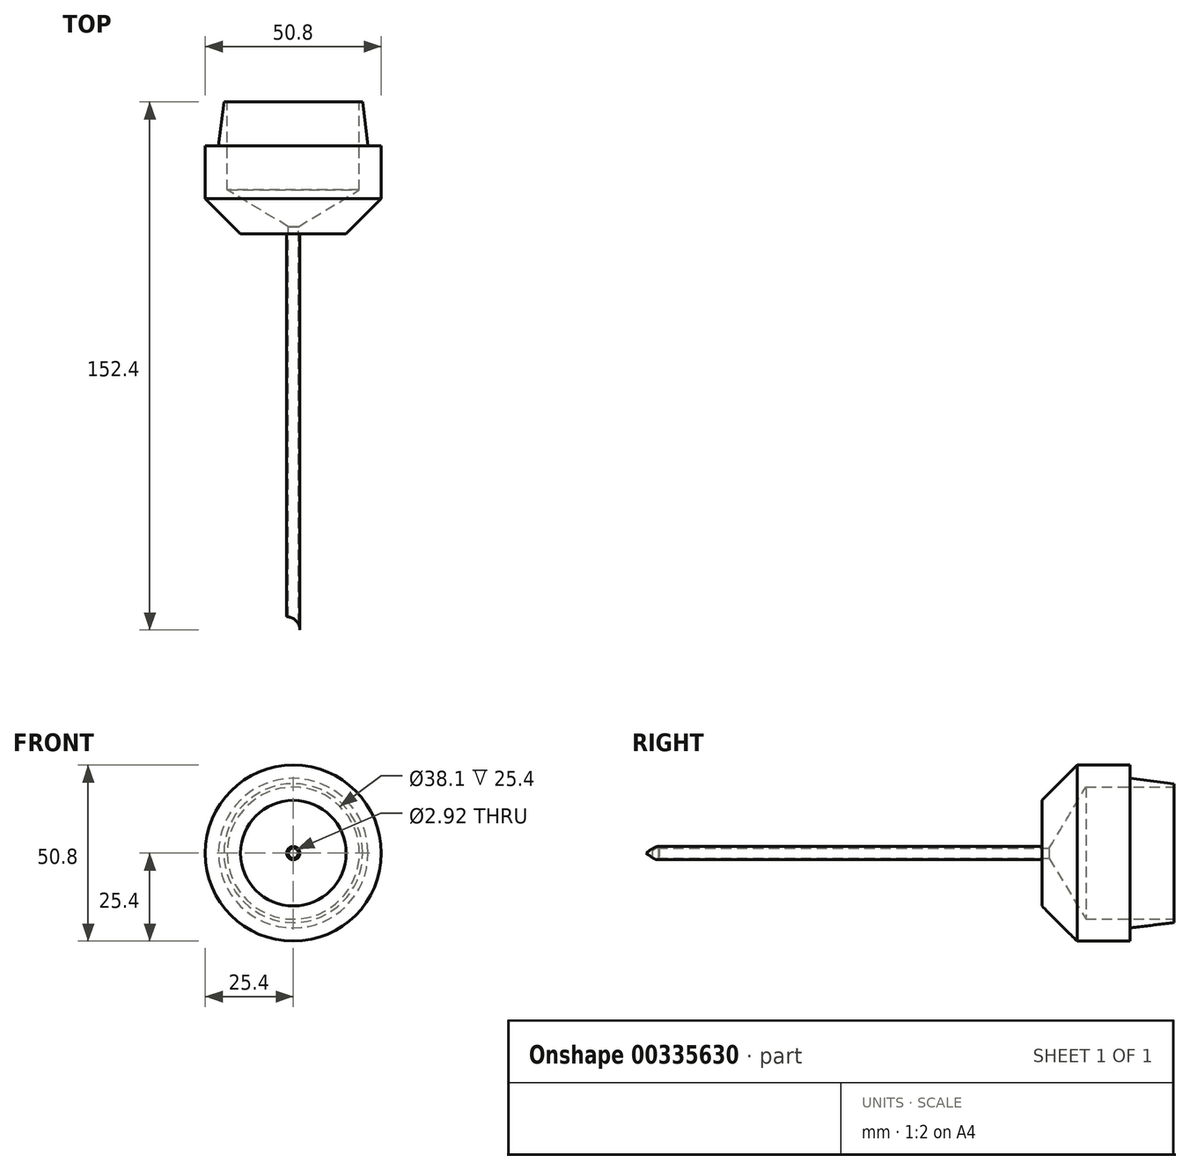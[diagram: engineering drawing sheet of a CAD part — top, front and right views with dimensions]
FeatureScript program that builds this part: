
annotation { "Feature Type Name" : "Feature", "Feature Type Description" : "" }
export const myFeature = defineFeature(function(context is Context, id is Id, definition is map)
    precondition{}
    {
        {
            var Q0;
            Q0=qCreatedBy(makeId("Front.planeOp"),FACE);
            var sketch = newSketch(context, id + "F0", { "sketchPlane" : qUnion([Q0])});
            skCircle(sketch, "E0", {"center": v(0, 0) * mm, "radius": 21.59 * mm});
            skSolve(sketch);
        }
        {
            var Q0;
            Q0 = qSketchRegion(id + "F0", true);
            extrude(context, id + "F1", {"entities" : qUnion([Q0]), "depth" : 12.7 * mm});
        }
        {
            var Q0;
            Q0=makeQuery(id+"F1.opExtrude","CAP_FACE",FACE,{"disambiguationData":[OSD([sQuery(id+"F0.wireOp",EDGE,"E0")])],"isStart":false});
            var sketch = newSketch(context, id + "F2", { "sketchPlane" : qUnion([Q0])});
            skCircle(sketch, "E1", {"center": v(0, 0) * mm, "radius": 25.4 * mm});
            skSolve(sketch);
        }
        {
            var Q0;
            Q0 = qSketchRegion(id + "F2", true);
            extrude(context, id + "F3", {"entities" : qUnion([Q0]), "operationType" : NewBodyOperationType.ADD, "depth" : 25.4 * mm});
        }
        {
            var Q0;
            Q0=makeQuery(id+"F3.opExtrude","CAP_EDGE",EDGE,{"disambiguationData":[OSD([sQuery(id+"F2.wireOp",EDGE,"E1")])],"isStart":false});
            chamfer(context, id + "F4", {"entities" : qUnion([Q0]), "width" : 10.16 * mm, "tangentPropagation" : true});
        }
        {
            var Q0;
            Q0=makeQuery(id+"F3.opExtrude","CAP_FACE",FACE,{"disambiguationData":[OSD([sQuery(id+"F2.wireOp",EDGE,"E1")])],"isStart":false});
            var sketch = newSketch(context, id + "F5", { "sketchPlane" : qUnion([Q0])});
            skLineSegment(sketch, "E2.bottom", {"start": v(1.9, -1.9) * mm, "end": v(-1.9, -1.9) * mm});
            skLineSegment(sketch, "E2.top", {"start": v(1.9, 1.9) * mm, "end": v(-1.9, 1.9) * mm});
            skLineSegment(sketch, "E2.left", {"start": v(1.9, -1.9) * mm, "end": v(1.9, 1.9) * mm});
            skLineSegment(sketch, "E2.right", {"start": v(-1.9, -1.9) * mm, "end": v(-1.9, 1.9) * mm});
            skPoint(sketch, "E2.middle", {"position": v(0, 0) * mm});
            skSolve(sketch);
        }
        {
            var Q0;
            Q0 = qSketchRegion(id + "F5", true);
            extrude(context, id + "F6", {"entities" : qUnion([Q0]), "operationType" : NewBodyOperationType.ADD, "depth" : 114.3 * mm});
        }
        {
            var Q0;
            Q0=makeQuery(id+"F6.opExtrude","SWEPT_FACE",FACE,{"disambiguationData":[OSD([sQuery(id+"F5.wireOp",EDGE,"E2.top")])]});
            var sketch = newSketch(context, id + "F7", { "sketchPlane" : qUnion([Q0])});
            skLineSegment(sketch, "E3", {"start": v(-1.9, -152.4) * mm, "end": v(-1.9, -173.93) * mm});
            skSolve(sketch);
        }
        {
            var Q0;
            Q0=sQuery(id+"F7.wireOp",VERTEX,"E3.start");
            var Q1;
            Q1=makeQuery(id+"F1.opExtrude","SWEPT_BODY",BODY,{"disambiguationData":[OSD([sQuery(id+"F0.wireOp",EDGE,"E0")])]});
            hole(context, id + "F8", {"style" : HoleStyle.SIMPLE, "endStyle" : HoleEndStyle.THROUGH, "holeDiameter" : 7.62 * mm, "tappedDepth" : 12.7 * mm, "tapClearance" : 3, "locations" : qUnion([Q0]), "scope" : qUnion([Q1])});
        }
        {
            var Q0;
            Q0=makeQuery(id+"F6.opExtrude","SWEPT_EDGE",EDGE,{"disambiguationData":[OSD([sQuery(id+"F5.wireOp",EDGE,"E2.bottom"),sQuery(id+"F5.wireOp",EDGE,"E2.left")])]});
            var Q1;
            Q1=makeQuery(id+"F6.opExtrude","SWEPT_EDGE",EDGE,{"disambiguationData":[OSD([sQuery(id+"F5.wireOp",EDGE,"E2.top"),sQuery(id+"F5.wireOp",EDGE,"E2.left")])]});
            var Q2;
            Q2=makeQuery(id+"F6.opExtrude","SWEPT_EDGE",EDGE,{"disambiguationData":[OSD([sQuery(id+"F5.wireOp",EDGE,"E2.top"),sQuery(id+"F5.wireOp",EDGE,"E2.right")])]});
            var Q3;
            Q3=makeQuery(id+"F6.opExtrude","SWEPT_EDGE",EDGE,{"disambiguationData":[OSD([sQuery(id+"F5.wireOp",EDGE,"E2.bottom"),sQuery(id+"F5.wireOp",EDGE,"E2.right")])]});
            fillet(context, id + "F9", {"entities" : qUnion([Q0, Q1, Q2, Q3]), "radius" : 1.9 * mm, "tangentPropagation" : true, "allowEdgeOverflow" : false});
        }
        {
            var Q0;
            Q0=makeQuery(id+"F1.opExtrude","CAP_FACE",FACE,{"disambiguationData":[OSD([sQuery(id+"F0.wireOp",EDGE,"E0")])],"isStart":true});
            var sketch = newSketch(context, id + "F10", { "sketchPlane" : qUnion([Q0])});
            skCircle(sketch, "E4", {"center": v(0, 0) * mm, "radius": 19.05 * mm});
            skSolve(sketch);
        }
        {
            var Q0;
            Q0=sQuery(id+"F10.wireOp",VERTEX,"E4.center");
            var Q1;
            Q1=makeQuery(id+"F1.opExtrude","SWEPT_BODY",BODY,{"disambiguationData":[OSD([sQuery(id+"F0.wireOp",EDGE,"E0")])]});
            hole(context, id + "F11", {"style" : HoleStyle.SIMPLE, "endStyle" : HoleEndStyle.BLIND, "holeDiameter" : 38.1 * mm, "holeDepth" : 25.4 * mm, "tappedDepth" : 12.7 * mm, "tapClearance" : 3, "locations" : qUnion([Q0]), "scope" : qUnion([Q1])});
        }
        {
            var Q0;
            Q0=qCreatedBy(makeId("Front.planeOp"),FACE);
            var sketch = newSketch(context, id + "F12", { "sketchPlane" : qUnion([Q0])});
            skCircle(sketch, "E5", {"center": v(0, 0) * mm, "radius": 1.46 * mm});
            skSolve(sketch);
        }
        {
            var Q0;
            Q0=sQuery(id+"F12.wireOp",VERTEX,"E5.center");
            var Q1;
            Q1=makeQuery(id+"F1.opExtrude","SWEPT_BODY",BODY,{"disambiguationData":[OSD([sQuery(id+"F0.wireOp",EDGE,"E0")])]});
            hole(context, id + "F13", {"style" : HoleStyle.SIMPLE, "endStyle" : HoleEndStyle.BLIND, "oppositeDirection" : true, "holeDiameter" : 2.92 * mm, "holeDepth" : 254 * mm, "tappedDepth" : 12.7 * mm, "tapClearance" : 3, "locations" : qUnion([Q0]), "scope" : qUnion([Q1])});
        }
        {
            var Q0;
            Q0=makeQuery(id+"F1.opExtrude","CAP_EDGE",EDGE,{"disambiguationData":[OSD([sQuery(id+"F0.wireOp",EDGE,"E0")])],"isStart":true});
            chamfer(context, id + "F14", {"entities" : qUnion([Q0]), "chamferType" : ChamferType.OFFSET_ANGLE, "width" : 12.7 * mm, "oppositeDirection" : false, "angle" : 7 * degree, "tangentPropagation" : true});
        }
    });
